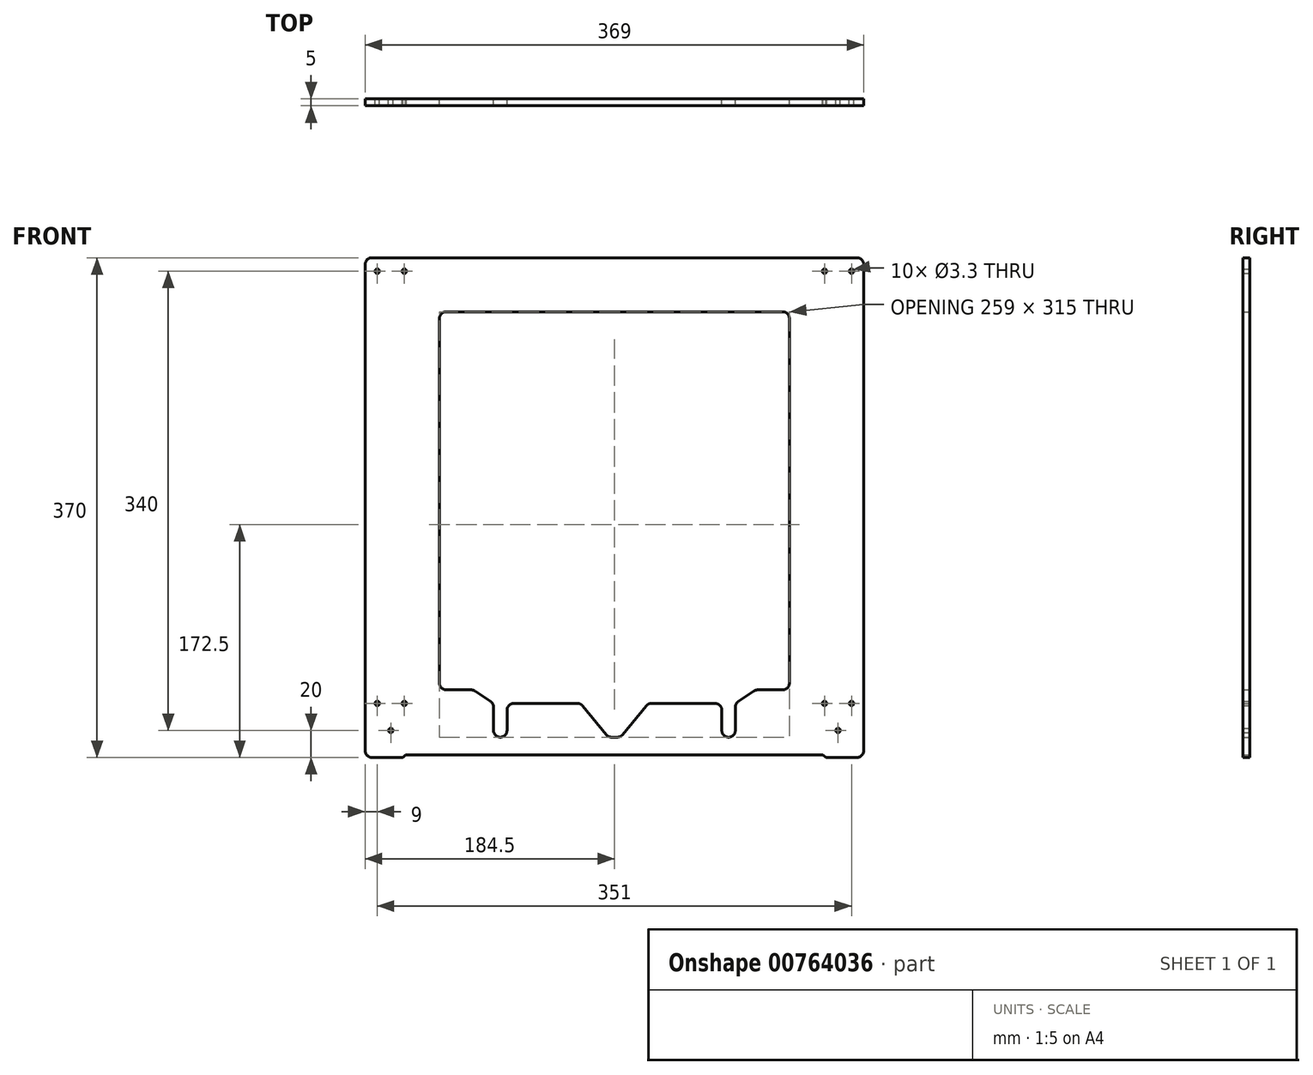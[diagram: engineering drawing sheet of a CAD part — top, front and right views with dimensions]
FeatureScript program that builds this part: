
annotation { "Feature Type Name" : "Feature", "Feature Type Description" : "" }
export const myFeature = defineFeature(function(context is Context, id is Id, definition is map)
    precondition{}
    {
        {
            var Q0;
            Q0=qCreatedBy(makeId("Front.planeOp"),FACE);
            var sketch = newSketch(context, id + "F0", { "sketchPlane" : qUnion([Q0])});
            skLineSegment(sketch, "E0.bottom", {"start": v(-179.5, 185) * mm, "end": v(179.5, 185) * mm});
            skLineSegment(sketch, "E0.top", {"start": v(-179.5, -185) * mm, "end": v(179.5, -185) * mm});
            skLineSegment(sketch, "E0.left", {"start": v(-184.5, 180) * mm, "end": v(-184.5, -180) * mm});
            skLineSegment(sketch, "E0.right", {"start": v(184.5, 180) * mm, "end": v(184.5, -180) * mm});
            skPoint(sketch, "E0.middle", {"position": v(0, 0) * mm});
            skLineSegment(sketch, "E1", {"start": v(0, 185) * mm, "end": v(0, -185) * mm, "construction": true});
            skLineSegment(sketch, "E2", {"start": v(-2.13, -170) * mm, "end": v(4.5, -170) * mm});
            skPoint(sketch, "E3", {"position": v(0, -170) * mm});
            skLineSegment(sketch, "E4", {"start": v(-27.37, -145) * mm, "end": v(-51.1, -145) * mm});
            skLineSegment(sketch, "E5", {"start": v(-23.5, -146.83) * mm, "end": v(-6, -168.17) * mm});
            skPoint(sketch, "E6", {"position": v(-84.5, -165) * mm});
            skCircle(sketch, "E7", {"center": v(-84.5, -165) * mm, "radius": 5 * mm});
            skLineSegment(sketch, "E8", {"start": v(-74.51, -145) * mm, "end": v(-51.1, -145) * mm});
            skLineSegment(sketch, "E9", {"start": v(-129.5, -130) * mm, "end": v(-129.5, -79.62) * mm});
            skLineSegment(sketch, "E10", {"start": v(-89.5, -165) * mm, "end": v(-89.5, -147.68) * mm});
            skLineSegment(sketch, "E11", {"start": v(-79.5, -165) * mm, "end": v(-79.51, -150) * mm});
            skLineSegment(sketch, "E12", {"start": v(-124.5, -135) * mm, "end": v(-106.01, -135) * mm});
            skLineSegment(sketch, "E13", {"start": v(-103.24, -135.84) * mm, "end": v(-91.73, -143.52) * mm});
            skPoint(sketch, "E14.visualSharp", {"position": v(-79.51, -145) * mm});
            skArc(sketch, "E14.filletArc", {"start": v(-74.51, -145) * mm, "mid": v(-78.05, -146.47) * mm, "end": v(-79.51, -150) * mm});
            skPoint(sketch, "E15.visualSharp", {"position": v(-89.5, -145) * mm});
            skArc(sketch, "E15.filletArc", {"start": v(-89.5, -147.68) * mm, "mid": v(-90.1, -145.32) * mm, "end": v(-91.73, -143.52) * mm});
            skPoint(sketch, "E16.visualSharp", {"position": v(-104.5, -135) * mm});
            skArc(sketch, "E16.filletArc", {"start": v(-103.24, -135.84) * mm, "mid": v(-104.56, -135.21) * mm, "end": v(-106.01, -135) * mm});
            skPoint(sketch, "E17.visualSharp", {"position": v(-129.5, -135) * mm});
            skArc(sketch, "E17.filletArc", {"start": v(-129.5, -130) * mm, "mid": v(-128.04, -133.54) * mm, "end": v(-124.5, -135) * mm});
            skPoint(sketch, "E18.visualSharp", {"position": v(-25, -145) * mm});
            skArc(sketch, "E18.filletArc", {"start": v(-23.5, -146.83) * mm, "mid": v(-25.23, -145.48) * mm, "end": v(-27.37, -145) * mm});
            skPoint(sketch, "E19.visualSharp", {"position": v(-4.5, -170) * mm});
            skArc(sketch, "E19.filletArc", {"start": v(-6, -168.17) * mm, "mid": v(-4.27, -169.52) * mm, "end": v(-2.13, -170) * mm});
            skLineSegment(sketch, "E20", {"start": v(0, 145) * mm, "end": v(-124.5, 145) * mm});
            skLineSegment(sketch, "E21", {"start": v(-129.5, 140) * mm, "end": v(-129.5, -79.62) * mm});
            skPoint(sketch, "E22.visualSharp", {"position": v(-129.5, 145) * mm});
            skArc(sketch, "E22.filletArc", {"start": v(-124.5, 145) * mm, "mid": v(-128.04, 143.54) * mm, "end": v(-129.5, 140) * mm});
            skPoint(sketch, "E23.visualSharp", {"position": v(-184.5, 185) * mm});
            skArc(sketch, "E23.filletArc", {"start": v(-179.5, 185) * mm, "mid": v(-183.04, 183.54) * mm, "end": v(-184.5, 180) * mm});
            skPoint(sketch, "E24.visualSharp", {"position": v(184.5, 185) * mm});
            skArc(sketch, "E24.filletArc", {"start": v(184.5, 180) * mm, "mid": v(183.04, 183.54) * mm, "end": v(179.5, 185) * mm});
            skPoint(sketch, "E25.visualSharp", {"position": v(184.5, -185) * mm});
            skArc(sketch, "E25.filletArc", {"start": v(179.5, -185) * mm, "mid": v(183.04, -183.54) * mm, "end": v(184.5, -180) * mm});
            skPoint(sketch, "E26.visualSharp", {"position": v(-184.5, -185) * mm});
            skArc(sketch, "E26.filletArc", {"start": v(-184.5, -180) * mm, "mid": v(-183.04, -183.54) * mm, "end": v(-179.5, -185) * mm});
            skLineSegment(sketch, "E27", {"start": v(-154.5, -183) * mm, "end": v(0, -183) * mm});
            skLineSegment(sketch, "E28", {"start": v(-154.5, -183) * mm, "end": v(-156.5, -185) * mm});
            skPoint(sketch, "E29", {"position": v(-165.5, -165) * mm});
            skPoint(sketch, "E30", {"position": v(-175.5, -145) * mm});
            skPoint(sketch, "E31", {"position": v(-155.5, -145) * mm});
            skPoint(sketch, "E32", {"position": v(-175.5, 175) * mm});
            skPoint(sketch, "E33", {"position": v(-155.5, 175) * mm});
            skArc(sketch, "E34.MirrorCS", {"start": v(74.51, -145) * mm, "mid": v(78.05, -146.47) * mm, "end": v(79.51, -150) * mm});
            skLineSegment(sketch, "E35.MirrorCS", {"start": v(154.5, -183) * mm, "end": v(156.5, -185) * mm});
            skArc(sketch, "E36.MirrorCS", {"start": v(89.5, -147.68) * mm, "mid": v(90.1, -145.32) * mm, "end": v(91.73, -143.52) * mm});
            skLineSegment(sketch, "E37.MirrorCS", {"start": v(79.5, -165) * mm, "end": v(79.51, -150) * mm});
            skLineSegment(sketch, "E38.MirrorCS", {"start": v(89.5, -165) * mm, "end": v(89.5, -147.68) * mm});
            skArc(sketch, "E39.MirrorCS", {"start": v(23.5, -146.83) * mm, "mid": v(25.23, -145.48) * mm, "end": v(27.37, -145) * mm});
            skArc(sketch, "E40.MirrorCS", {"start": v(179.5, 185) * mm, "mid": v(183.04, 183.54) * mm, "end": v(184.5, 180) * mm});
            skLineSegment(sketch, "E41.MirrorCS", {"start": v(124.5, -135) * mm, "end": v(106.01, -135) * mm});
            skLineSegment(sketch, "E42.MirrorCS", {"start": v(103.24, -135.84) * mm, "end": v(91.73, -143.52) * mm});
            skArc(sketch, "E43.MirrorCS", {"start": v(103.24, -135.84) * mm, "mid": v(104.56, -135.21) * mm, "end": v(106.01, -135) * mm});
            skLineSegment(sketch, "E44.MirrorCS", {"start": v(2.13, -170) * mm, "end": v(-4.5, -170) * mm});
            skArc(sketch, "E45.MirrorCS", {"start": v(129.5, -130) * mm, "mid": v(128.04, -133.54) * mm, "end": v(124.5, -135) * mm});
            skArc(sketch, "E46.MirrorCS", {"start": v(6, -168.17) * mm, "mid": v(4.27, -169.52) * mm, "end": v(2.13, -170) * mm});
            skCircle(sketch, "E47.MirrorC", {"center": v(84.5, -165) * mm, "radius": 5 * mm});
            skArc(sketch, "E48.MirrorCS", {"start": v(124.5, 145) * mm, "mid": v(128.04, 143.54) * mm, "end": v(129.5, 140) * mm});
            skArc(sketch, "E49.MirrorCS", {"start": v(184.5, -180) * mm, "mid": v(183.04, -183.54) * mm, "end": v(179.5, -185) * mm});
            skLineSegment(sketch, "E50.MirrorCS", {"start": v(23.5, -146.83) * mm, "end": v(6, -168.17) * mm});
            skLineSegment(sketch, "E51.MirrorCS", {"start": v(27.37, -145) * mm, "end": v(51.1, -145) * mm});
            skLineSegment(sketch, "E52.MirrorCS", {"start": v(74.51, -145) * mm, "end": v(51.1, -145) * mm});
            skPoint(sketch, "E53.MirrorP", {"position": v(165.5, -165) * mm});
            skLineSegment(sketch, "E54.MirrorCS", {"start": v(154.5, -183) * mm, "end": v(0, -183) * mm});
            skPoint(sketch, "E55.MirrorP", {"position": v(129.5, 145) * mm});
            skLineSegment(sketch, "E56.MirrorCS", {"start": v(0, 145) * mm, "end": v(124.5, 145) * mm});
            skLineSegment(sketch, "E57.MirrorCS", {"start": v(179.5, 185) * mm, "end": v(-179.5, 185) * mm});
            skLineSegment(sketch, "E58.MirrorCS", {"start": v(179.5, -185) * mm, "end": v(-179.5, -185) * mm});
            skPoint(sketch, "E59.MirrorP", {"position": v(155.5, 175) * mm});
            skPoint(sketch, "E60.MirrorP", {"position": v(4.5, -170) * mm});
            skPoint(sketch, "E61.MirrorP", {"position": v(25, -145) * mm});
            skPoint(sketch, "E62.MirrorP", {"position": v(129.5, -135) * mm});
            skPoint(sketch, "E63.MirrorP", {"position": v(155.5, -145) * mm});
            skPoint(sketch, "E64.MirrorP", {"position": v(104.5, -135) * mm});
            skLineSegment(sketch, "E65.MirrorCS", {"start": v(129.5, 140) * mm, "end": v(129.5, -79.62) * mm});
            skPoint(sketch, "E66.MirrorP", {"position": v(89.5, -145) * mm});
            skPoint(sketch, "E67.MirrorP", {"position": v(79.51, -145) * mm});
            skPoint(sketch, "E68.MirrorP", {"position": v(175.5, 175) * mm});
            skLineSegment(sketch, "E69.MirrorCS", {"start": v(129.5, -130) * mm, "end": v(129.5, -79.62) * mm});
            skPoint(sketch, "E70.MirrorP", {"position": v(175.5, -145) * mm});
            skSolve(sketch);
        }
        {
            var Q0;
            Q0=makeQuery(id+"F0.imprint","IMPRINT",FACE,{"disambiguationData":[TD([[makeQuery(id+"F0.imprint","IMPRINT",EDGE,{"derivedFrom":sQuery(id+"F0.wireOp",EDGE,"E0.left")}),1.0]])]});
            extrude(context, id + "F1", {"entities" : qUnion([Q0]), "depth" : 5 * mm, "offsetDistance" : 25 * mm});
        }
        {
            var Q0;
            Q0=sQuery(id+"F0.wireOp",VERTEX,"E32");
            var Q1;
            Q1=sQuery(id+"F0.wireOp",VERTEX,"E33");
            var Q2;
            Q2=sQuery(id+"F0.wireOp",VERTEX,"E30");
            var Q3;
            Q3=sQuery(id+"F0.wireOp",VERTEX,"E31");
            var Q4;
            Q4=sQuery(id+"F0.wireOp",VERTEX,"E29");
            var Q5;
            Q5=sQuery(id+"F0.wireOp",VERTEX,"E59.MirrorP");
            var Q6;
            Q6=sQuery(id+"F0.wireOp",VERTEX,"E68.MirrorP");
            var Q7;
            Q7=sQuery(id+"F0.wireOp",VERTEX,"E63.MirrorP");
            var Q8;
            Q8=sQuery(id+"F0.wireOp",VERTEX,"E70.MirrorP");
            var Q9;
            Q9=sQuery(id+"F0.wireOp",VERTEX,"E53.MirrorP");
            var Q10;
            Q10=makeQuery(id+"F1.opExtrude","SWEPT_BODY",BODY,{"disambiguationData":[OSD([sQuery(id+"F0.wireOp",EDGE,"E0.left"),sQuery(id+"F0.wireOp",EDGE,"E4"),sQuery(id+"F0.wireOp",EDGE,"E5"),sQuery(id+"F0.wireOp",EDGE,"E7"),sQuery(id+"F0.wireOp",EDGE,"E8"),sQuery(id+"F0.wireOp",EDGE,"E9"),sQuery(id+"F0.wireOp",EDGE,"E10"),sQuery(id+"F0.wireOp",EDGE,"E11"),sQuery(id+"F0.wireOp",EDGE,"E12"),sQuery(id+"F0.wireOp",EDGE,"E13"),sQuery(id+"F0.wireOp",EDGE,"E14.filletArc"),sQuery(id+"F0.wireOp",EDGE,"E15.filletArc"),sQuery(id+"F0.wireOp",EDGE,"E16.filletArc"),sQuery(id+"F0.wireOp",EDGE,"E17.filletArc"),sQuery(id+"F0.wireOp",EDGE,"E18.filletArc"),sQuery(id+"F0.wireOp",EDGE,"E19.filletArc"),sQuery(id+"F0.wireOp",EDGE,"E20"),sQuery(id+"F0.wireOp",EDGE,"E21"),sQuery(id+"F0.wireOp",EDGE,"E22.filletArc"),sQuery(id+"F0.wireOp",EDGE,"E23.filletArc"),sQuery(id+"F0.wireOp",EDGE,"E26.filletArc"),sQuery(id+"F0.wireOp",EDGE,"E27"),sQuery(id+"F0.wireOp",EDGE,"E28"),sQuery(id+"F0.wireOp",EDGE,"E34.MirrorCS"),sQuery(id+"F0.wireOp",EDGE,"E35.MirrorCS"),sQuery(id+"F0.wireOp",EDGE,"E36.MirrorCS"),sQuery(id+"F0.wireOp",EDGE,"E37.MirrorCS"),sQuery(id+"F0.wireOp",EDGE,"E38.MirrorCS"),sQuery(id+"F0.wireOp",EDGE,"E39.MirrorCS"),sQuery(id+"F0.wireOp",EDGE,"E40.MirrorCS"),sQuery(id+"F0.wireOp",EDGE,"E41.MirrorCS"),sQuery(id+"F0.wireOp",EDGE,"E42.MirrorCS"),sQuery(id+"F0.wireOp",EDGE,"E43.MirrorCS"),sQuery(id+"F0.wireOp",EDGE,"E44.MirrorCS"),sQuery(id+"F0.wireOp",EDGE,"E45.MirrorCS"),sQuery(id+"F0.wireOp",EDGE,"E46.MirrorCS"),sQuery(id+"F0.wireOp",EDGE,"E47.MirrorC"),sQuery(id+"F0.wireOp",EDGE,"E48.MirrorCS"),sQuery(id+"F0.wireOp",EDGE,"E49.MirrorCS"),sQuery(id+"F0.wireOp",EDGE,"E50.MirrorCS"),sQuery(id+"F0.wireOp",EDGE,"E51.MirrorCS"),sQuery(id+"F0.wireOp",EDGE,"E52.MirrorCS"),sQuery(id+"F0.wireOp",EDGE,"E54.MirrorCS"),sQuery(id+"F0.wireOp",EDGE,"E56.MirrorCS"),sQuery(id+"F0.wireOp",EDGE,"E57.MirrorCS"),sQuery(id+"F0.wireOp",EDGE,"E58.MirrorCS"),sQuery(id+"F0.wireOp",EDGE,"E0.right"),sQuery(id+"F0.wireOp",EDGE,"E65.MirrorCS"),sQuery(id+"F0.wireOp",EDGE,"E69.MirrorCS")])]});
            hole(context, id + "F2", {"style" : HoleStyle.SIMPLE, "endStyle" : HoleEndStyle.BLIND, "oppositeDirection" : true, "standardTappedOrClearance" : lookupTablePath({ "standard" : "ISO", "fit" : "Normal", "size" : "M3", "type" : "Clearance" }), "standardBlindInLast" : lookupTablePath({ "fit" : "Standard", "standard" : "ISO", "size" : "M3", "type" : "Clearance" }), "holeDiameter" : 3.3 * mm, "majorDiameter" : 5 * mm, "holeDepth" : 10 * mm, "isTappedThrough" : true, "tappedDepth" : 12 * mm, "tapClearance" : 3, "locations" : qUnion([Q0, Q1, Q2, Q3, Q4, Q5, Q6, Q7, Q8, Q9]), "scope" : qUnion([Q10])});
        }
    });
